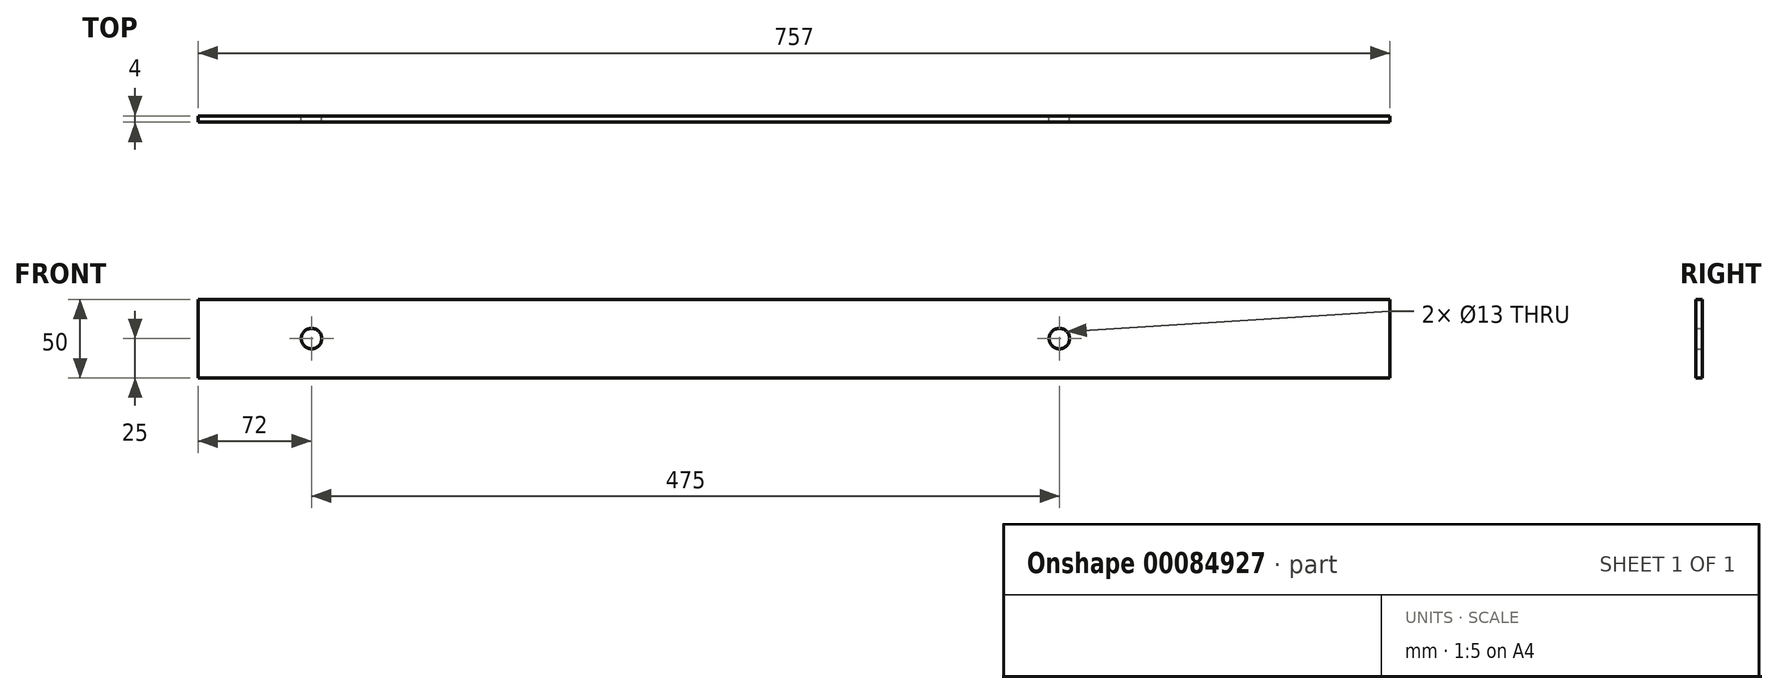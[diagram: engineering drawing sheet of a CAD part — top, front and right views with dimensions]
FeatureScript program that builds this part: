
annotation { "Feature Type Name" : "Feature", "Feature Type Description" : "" }
export const myFeature = defineFeature(function(context is Context, id is Id, definition is map)
    precondition{}
    {
        {
            var Q0;
            Q0=qCreatedBy(makeId("Front.planeOp"),FACE);
            var sketch = newSketch(context, id + "F0", { "sketchPlane" : qUnion([Q0])});
            skLineSegment(sketch, "E0.bottom", {"start": v(0, 0) * mm, "end": v(757, 0) * mm});
            skLineSegment(sketch, "E0.top", {"start": v(0, 50) * mm, "end": v(757, 50) * mm});
            skLineSegment(sketch, "E0.left", {"start": v(0, 0) * mm, "end": v(0, 50) * mm});
            skLineSegment(sketch, "E0.right", {"start": v(757, 0) * mm, "end": v(757, 50) * mm});
            skCircle(sketch, "E1", {"center": v(72, 25) * mm, "radius": 6.5 * mm});
            skPoint(sketch, "E1.centerSnap0", {"position": v(0, 25) * mm});
            skCircle(sketch, "E2", {"center": v(547, 25) * mm, "radius": 6.5 * mm});
            skPoint(sketch, "E2.centerSnap0", {"position": v(757, 25) * mm});
            skSolve(sketch);
        }
        {
            var Q0;
            Q0=makeQuery(id+"F0.imprint","IMPRINT",FACE,{"disambiguationData":[TD([[makeQuery(id+"F0.imprint","IMPRINT",EDGE,{"derivedFrom":sQuery(id+"F0.wireOp",EDGE,"E0.bottom")}),1.0]])]});
            extrude(context, id + "F1", {"entities" : qUnion([Q0]), "depth" : 4 * mm});
        }
    });
